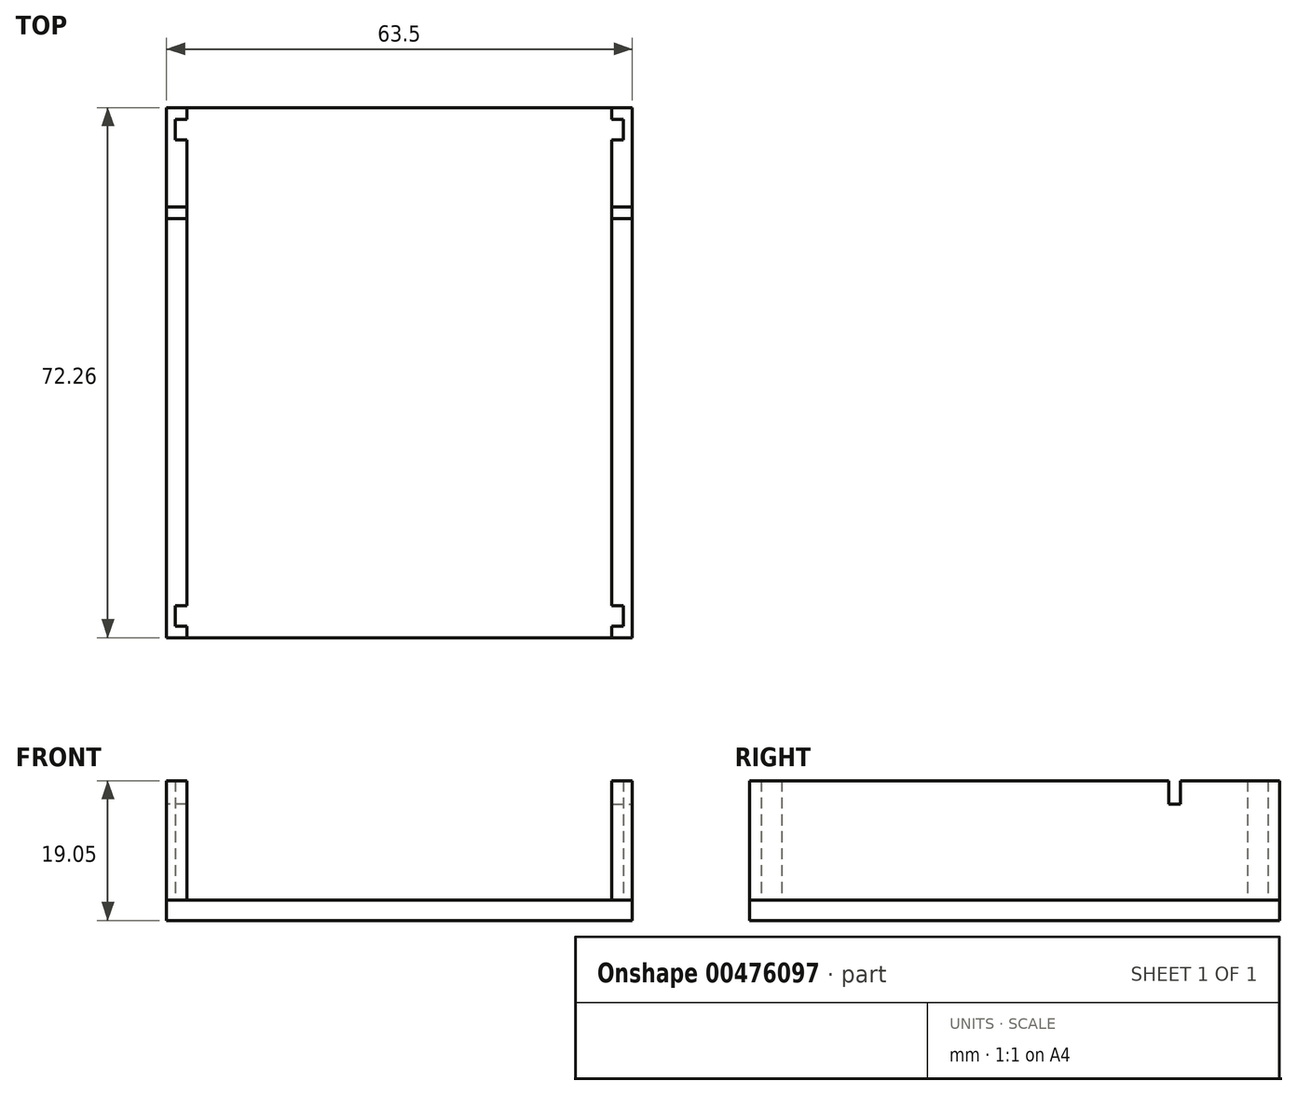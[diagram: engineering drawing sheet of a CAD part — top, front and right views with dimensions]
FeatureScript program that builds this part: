
annotation { "Feature Type Name" : "Feature", "Feature Type Description" : "" }
export const myFeature = defineFeature(function(context is Context, id is Id, definition is map)
    precondition{}
    {
        {
            var Q0;
            Q0=qCreatedBy(makeId("Top.planeOp"),FACE);
            var sketch = newSketch(context, id + "F0", { "sketchPlane" : qUnion([Q0])});
            skLineSegment(sketch, "E0.bottom", {"start": v(31.75, -36.13) * mm, "end": v(-31.75, -36.13) * mm});
            skLineSegment(sketch, "E0.top", {"start": v(31.75, 36.13) * mm, "end": v(-31.75, 36.13) * mm});
            skLineSegment(sketch, "E0.left", {"start": v(31.75, -36.13) * mm, "end": v(31.75, 36.13) * mm});
            skLineSegment(sketch, "E0.right", {"start": v(-31.75, -36.13) * mm, "end": v(-31.75, 36.13) * mm});
            skPoint(sketch, "E0.middle", {"position": v(0, 0) * mm});
            skSolve(sketch);
        }
        {
            var Q0;
            Q0=makeQuery(id+"F0.imprint","IMPRINT",FACE,{"disambiguationData":[TD([[makeQuery(id+"F0.imprint","IMPRINT",EDGE,{"derivedFrom":sQuery(id+"F0.wireOp",EDGE,"E0.bottom")}),-1.0]])]});
            extrude(context, id + "F1", {"entities" : qUnion([Q0]), "depth" : 2.8 * mm, "offsetDistance" : 25.4 * mm});
        }
        {
            var Q0;
            Q0=makeQuery(id+"F1.opExtrude","CAP_FACE",FACE,{"disambiguationData":[OSD([sQuery(id+"F0.wireOp",EDGE,"E0.bottom"),sQuery(id+"F0.wireOp",EDGE,"E0.top"),sQuery(id+"F0.wireOp",EDGE,"E0.left"),sQuery(id+"F0.wireOp",EDGE,"E0.right")])],"isStart":false});
            var sketch = newSketch(context, id + "F2", { "sketchPlane" : qUnion([Q0])});
            skLineSegment(sketch, "E1", {"start": v(28.96, 34.54) * mm, "end": v(28.96, 36.13) * mm});
            skLineSegment(sketch, "E2", {"start": v(28.96, 31.75) * mm, "end": v(28.96, -31.75) * mm});
            skLineSegment(sketch, "E3", {"start": v(28.96, -34.54) * mm, "end": v(28.96, -36.13) * mm});
            skLineSegment(sketch, "E4", {"start": v(30.54, -31.75) * mm, "end": v(30.54, -34.54) * mm});
            skLineSegment(sketch, "E5", {"start": v(28.96, -34.54) * mm, "end": v(30.54, -34.54) * mm});
            skLineSegment(sketch, "E6", {"start": v(28.96, -31.75) * mm, "end": v(30.54, -31.75) * mm});
            skLineSegment(sketch, "E7", {"start": v(28.96, 34.54) * mm, "end": v(30.54, 34.54) * mm});
            skLineSegment(sketch, "E8", {"start": v(30.54, 34.54) * mm, "end": v(30.54, 31.75) * mm});
            skLineSegment(sketch, "E9", {"start": v(30.54, 31.75) * mm, "end": v(28.96, 31.75) * mm});
            skSolve(sketch);
        }
        {
            var Q0;
            {var subQ1=sQuery(id+"F2.wireOp",EDGE,"E1");Q0=makeQuery(id+"F2.imprint","IMPRINT",FACE,{"disambiguationData":[TD([[makeQuery(id+"F2.imprint","IMPRINT",EDGE,{"derivedFrom":subQ1}),-1.0]])]});}
            extrude(context, id + "F3", {"entities" : qUnion([Q0]), "depth" : 16.26 * mm, "offsetDistance" : 25.4 * mm});
        }
        {
            var Q0;
            Q0=makeQuery(id+"F1.opExtrude","CAP_FACE",FACE,{"disambiguationData":[OSD([sQuery(id+"F0.wireOp",EDGE,"E0.bottom"),sQuery(id+"F0.wireOp",EDGE,"E0.top"),sQuery(id+"F0.wireOp",EDGE,"E0.left"),sQuery(id+"F0.wireOp",EDGE,"E0.right")])],"isStart":false});
            var sketch = newSketch(context, id + "F4", { "sketchPlane" : qUnion([Q0])});
            skLineSegment(sketch, "E10", {"start": v(-28.96, -36.13) * mm, "end": v(-28.96, -34.54) * mm});
            skLineSegment(sketch, "E11", {"start": v(-28.96, -34.54) * mm, "end": v(-30.54, -34.54) * mm});
            skLineSegment(sketch, "E12", {"start": v(-30.54, -34.54) * mm, "end": v(-30.54, -31.75) * mm});
            skLineSegment(sketch, "E13", {"start": v(-30.54, -31.75) * mm, "end": v(-28.96, -31.75) * mm});
            skLineSegment(sketch, "E14", {"start": v(-28.96, -31.75) * mm, "end": v(-28.96, 31.75) * mm});
            skLineSegment(sketch, "E15", {"start": v(-28.96, 31.75) * mm, "end": v(-30.54, 31.75) * mm});
            skLineSegment(sketch, "E16", {"start": v(-30.54, 31.75) * mm, "end": v(-30.54, 34.54) * mm});
            skLineSegment(sketch, "E17", {"start": v(-30.54, 34.54) * mm, "end": v(-28.96, 34.54) * mm});
            skLineSegment(sketch, "E18", {"start": v(-28.96, 34.54) * mm, "end": v(-28.96, 36.13) * mm});
            skSolve(sketch);
        }
        {
            var Q0;
            {var subQ2=sQuery(id+"F4.wireOp",EDGE,"E10");Q0=makeQuery(id+"F4.imprint","IMPRINT",FACE,{"disambiguationData":[TD([[makeQuery(id+"F4.imprint","IMPRINT",EDGE,{"derivedFrom":subQ2}),1.0]])]});}
            extrude(context, id + "F5", {"entities" : qUnion([Q0]), "depth" : 16.26 * mm, "offsetDistance" : 25.4 * mm});
        }
        {
            var Q0;
            Q0=makeQuery(id+"F3.opExtrude","SWEPT_FACE",FACE,{"disambiguationData":[OSD([sQuery(id+"F0.wireOp",EDGE,"E0.left")])]});
            var sketch = newSketch(context, id + "F6", { "sketchPlane" : qUnion([Q0])});
            skLineSegment(sketch, "E19", {"start": v(21, 19.05) * mm, "end": v(21, 15.88) * mm});
            skLineSegment(sketch, "E20", {"start": v(21, 15.88) * mm, "end": v(22.59, 15.88) * mm});
            skLineSegment(sketch, "E21", {"start": v(22.59, 15.88) * mm, "end": v(22.59, 19.05) * mm});
            skSolve(sketch);
        }
        {
            var Q0;
            {var subQ0=sQuery(id+"F6.wireOp",EDGE,"E19");Q0=makeQuery(id+"F6.imprint","IMPRINT",FACE,{"disambiguationData":[TD([[makeQuery(id+"F6.imprint","IMPRINT",EDGE,{"derivedFrom":subQ0}),1.0]])]});}
            var Q1;
            Q1=makeQuery(id+"F3.opExtrude","SWEPT_FACE",FACE,{"disambiguationData":[OSD([sQuery(id+"F2.wireOp",EDGE,"E2")])]});
            extrude(context, id + "F7", {"entities" : qUnion([Q0]), "operationType" : NewBodyOperationType.REMOVE, "endBound" : BoundingType.UP_TO_SURFACE, "oppositeDirection" : true, "depth" : 76.2 * mm, "endBoundEntityFace" : qUnion([Q1]), "offsetDistance" : 25.4 * mm});
        }
        {
            var Q0;
            Q0=makeQuery(id+"F5.opExtrude","SWEPT_FACE",FACE,{"disambiguationData":[OSD([sQuery(id+"F0.wireOp",EDGE,"E0.right")])]});
            var sketch = newSketch(context, id + "F8", { "sketchPlane" : qUnion([Q0])});
            skLineSegment(sketch, "E22", {"start": v(-22.59, 19.05) * mm, "end": v(-22.59, 15.88) * mm});
            skLineSegment(sketch, "E23", {"start": v(-22.59, 15.88) * mm, "end": v(-21, 15.88) * mm});
            skLineSegment(sketch, "E24", {"start": v(-21, 15.88) * mm, "end": v(-21, 19.05) * mm});
            skSolve(sketch);
        }
        {
            var Q0;
            {var subQ0=sQuery(id+"F8.wireOp",EDGE,"E22");Q0=makeQuery(id+"F8.imprint","IMPRINT",FACE,{"disambiguationData":[TD([[makeQuery(id+"F8.imprint","IMPRINT",EDGE,{"derivedFrom":subQ0}),1.0]])]});}
            var Q1;
            Q1=makeQuery(id+"F5.opExtrude","SWEPT_FACE",FACE,{"disambiguationData":[OSD([sQuery(id+"F4.wireOp",EDGE,"E14")])]});
            extrude(context, id + "F9", {"entities" : qUnion([Q0]), "operationType" : NewBodyOperationType.REMOVE, "endBound" : BoundingType.UP_TO_SURFACE, "oppositeDirection" : true, "depth" : 25.4 * mm, "endBoundEntityFace" : qUnion([Q1]), "offsetDistance" : 25.4 * mm});
        }
    });
